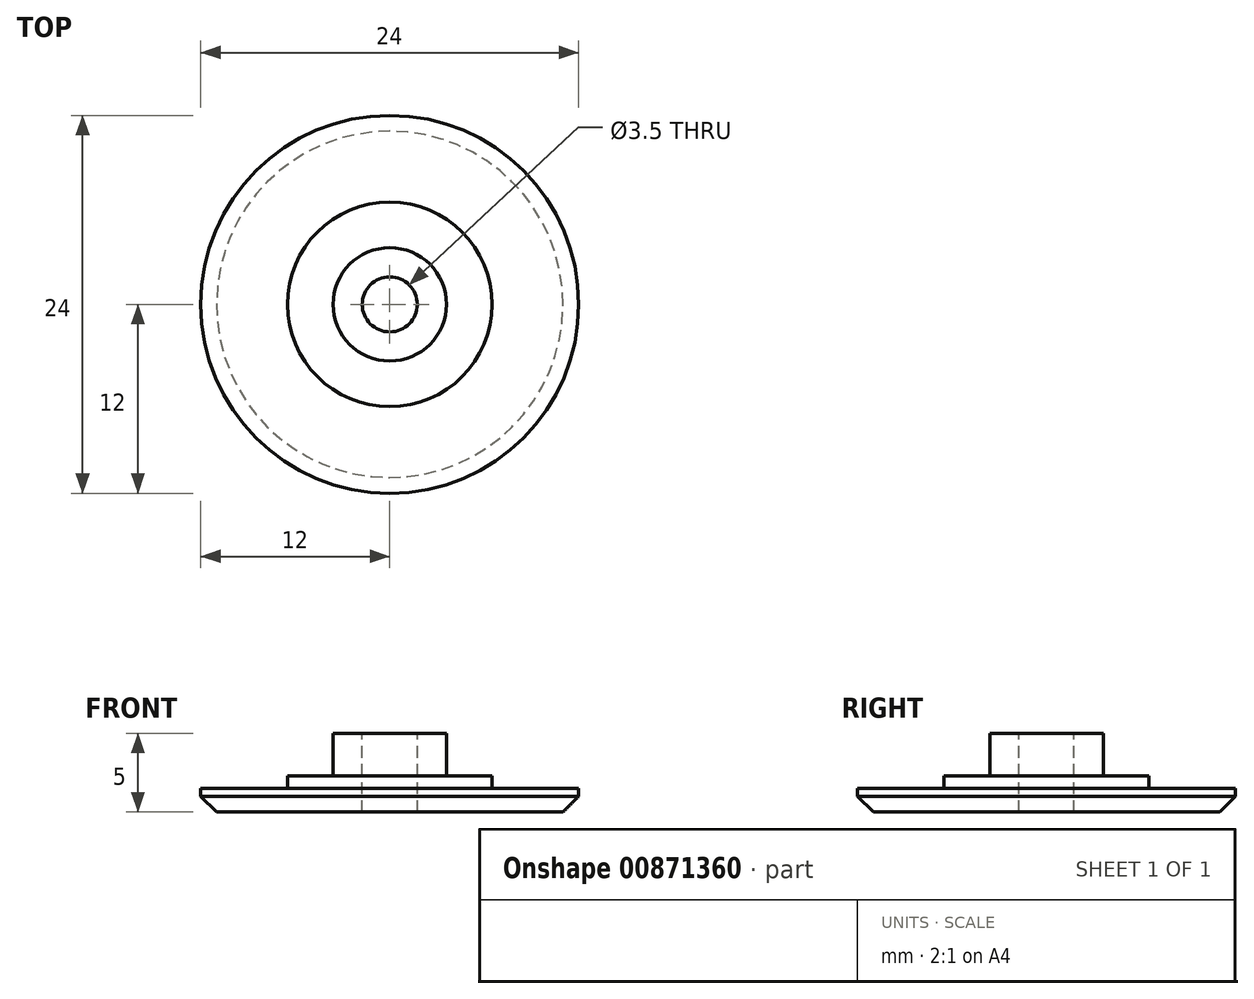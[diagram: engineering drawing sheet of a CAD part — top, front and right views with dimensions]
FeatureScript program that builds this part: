
annotation { "Feature Type Name" : "Feature", "Feature Type Description" : "" }
export const myFeature = defineFeature(function(context is Context, id is Id, definition is map)
    precondition{}
    {
        {
            var Q0;
            Q0=qCreatedBy(makeId("Top.planeOp"),FACE);
            var sketch = newSketch(context, id + "F0", { "sketchPlane" : qUnion([Q0])});
            skCircle(sketch, "E0", {"center": v(0, 0) * mm, "radius": 12 * mm});
            skCircle(sketch, "E1", {"center": v(0, 0) * mm, "radius": 3.6 * mm});
            skCircle(sketch, "E2", {"center": v(0, 0) * mm, "radius": 1.75 * mm});
            skCircle(sketch, "E3", {"center": v(0, 0) * mm, "radius": 6.5 * mm});
            skSolve(sketch);
        }
        {
            var Q0;
            Q0=makeQuery(id+"F0.imprint","IMPRINT",FACE,{"disambiguationData":[TD([[makeQuery(id+"F0.imprint","IMPRINT",EDGE,{"derivedFrom":sQuery(id+"F0.wireOp",EDGE,"E0")}),1.0]])]});
            var Q1;
            Q1=makeQuery(id+"F0.imprint","IMPRINT",FACE,{"disambiguationData":[TD([[makeQuery(id+"F0.imprint","IMPRINT",EDGE,{"derivedFrom":sQuery(id+"F0.wireOp",EDGE,"E1")}),1.0]])]});
            var Q2;
            Q2=makeQuery(id+"F0.imprint","IMPRINT",FACE,{"disambiguationData":[TD([[makeQuery(id+"F0.imprint","IMPRINT",EDGE,{"derivedFrom":sQuery(id+"F0.wireOp",EDGE,"E1")}),-1.0]])]});
            extrude(context, id + "F1", {"entities" : qUnion([Q0, Q1, Q2]), "oppositeDirection" : true, "depth" : 1.5 * mm, "offsetDistance" : 25 * mm});
        }
        {
            var Q0;
            Q0=makeQuery(id+"F0.imprint","IMPRINT",FACE,{"disambiguationData":[TD([[makeQuery(id+"F0.imprint","IMPRINT",EDGE,{"derivedFrom":sQuery(id+"F0.wireOp",EDGE,"E1")}),1.0]])]});
            extrude(context, id + "F2", {"entities" : qUnion([Q0]), "operationType" : NewBodyOperationType.ADD, "depth" : 3.5 * mm, "offsetDistance" : 25 * mm});
        }
        {
            var Q0;
            Q0=makeQuery(id+"F0.imprint","IMPRINT",FACE,{"disambiguationData":[TD([[makeQuery(id+"F0.imprint","IMPRINT",EDGE,{"derivedFrom":sQuery(id+"F0.wireOp",EDGE,"E1")}),-1.0]])]});
            extrude(context, id + "F3", {"entities" : qUnion([Q0]), "operationType" : NewBodyOperationType.ADD, "depth" : 0.8 * mm, "offsetDistance" : 25 * mm});
        }
        {
            var Q0;
            Q0=makeQuery(id+"F1.opExtrude","CAP_EDGE",EDGE,{"disambiguationData":[OSD([sQuery(id+"F0.wireOp",EDGE,"E0")])],"isStart":false});
            chamfer(context, id + "F4", {"entities" : qUnion([Q0]), "width" : 1 * mm, "tangentPropagation" : true});
        }
    });
